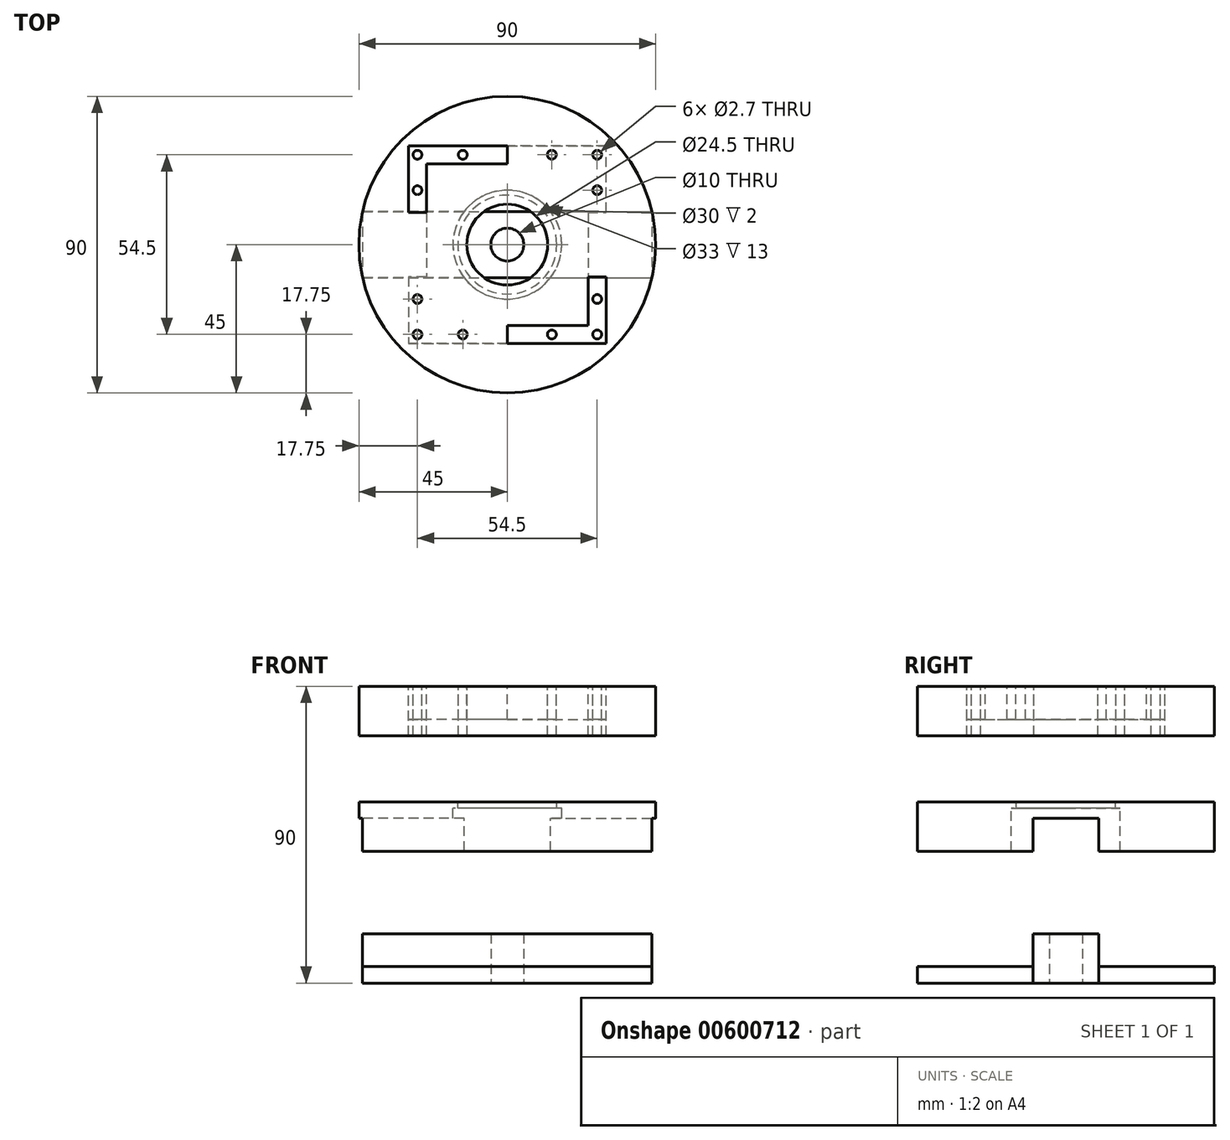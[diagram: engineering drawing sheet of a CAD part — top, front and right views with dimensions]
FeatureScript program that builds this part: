
annotation { "Feature Type Name" : "Feature", "Feature Type Description" : "" }
export const myFeature = defineFeature(function(context is Context, id is Id, definition is map)
    precondition{}
    {
        {
            var Q0;
            Q0=qCreatedBy(makeId("Top.planeOp"),FACE);
            var sketch = newSketch(context, id + "F0", { "sketchPlane" : qUnion([Q0])});
            skLineSegment(sketch, "E0.bottom", {"start": v(12.25, 0) * mm, "end": v(24.5, 0) * mm});
            skLineSegment(sketch, "E0.top", {"start": v(0, 24.5) * mm, "end": v(24.5, 24.5) * mm});
            skLineSegment(sketch, "E0.left", {"start": v(0, 12.25) * mm, "end": v(0, 24.5) * mm});
            skLineSegment(sketch, "E0.right", {"start": v(24.5, 0) * mm, "end": v(24.5, 24.5) * mm});
            skLineSegment(sketch, "E1", {"start": v(0, 24.5) * mm, "end": v(0, 30) * mm});
            skLineSegment(sketch, "E2", {"start": v(0, 30) * mm, "end": v(30, 30) * mm});
            skLineSegment(sketch, "E3", {"start": v(30, 30) * mm, "end": v(30, 9.75) * mm});
            skLineSegment(sketch, "E4", {"start": v(30, 9.75) * mm, "end": v(24.5, 9.75) * mm});
            skCircle(sketch, "E5", {"center": v(0, 0) * mm, "radius": 12.25 * mm});
            skLineSegment(sketch, "E6", {"start": v(0, 27.25) * mm, "end": v(38.5, 27.25) * mm, "construction": true});
            skLineSegment(sketch, "E7", {"start": v(27.25, 9.75) * mm, "end": v(27.25, 36.61) * mm, "construction": true});
            skCircle(sketch, "E8", {"center": v(27.25, 27.25) * mm, "radius": 1.35 * mm});
            skCircle(sketch, "E9", {"center": v(27.25, 16.5) * mm, "radius": 1.35 * mm});
            skCircle(sketch, "E10", {"center": v(13.5, 27.25) * mm, "radius": 1.35 * mm});
            skLineSegment(sketch, "E11.MirrorCS", {"start": v(-30, 30) * mm, "end": v(-30, 9.75) * mm});
            skLineSegment(sketch, "E12.MirrorCS", {"start": v(-24.5, 0) * mm, "end": v(-24.5, 24.5) * mm});
            skLineSegment(sketch, "E13.MirrorCS", {"start": v(-30, 9.75) * mm, "end": v(-24.5, 9.75) * mm});
            skCircle(sketch, "E14.MirrorC", {"center": v(-27.25, 16.5) * mm, "radius": 1.35 * mm});
            skCircle(sketch, "E15.MirrorC", {"center": v(-27.25, 27.25) * mm, "radius": 1.35 * mm});
            skCircle(sketch, "E16.MirrorC", {"center": v(-13.5, 27.25) * mm, "radius": 1.35 * mm});
            skLineSegment(sketch, "E17.MirrorCS", {"start": v(0, 30) * mm, "end": v(-30, 30) * mm});
            skLineSegment(sketch, "E18.MirrorCS", {"start": v(0, 24.5) * mm, "end": v(-24.5, 24.5) * mm});
            skLineSegment(sketch, "E19.MirrorCS", {"start": v(-30, -9.75) * mm, "end": v(-24.5, -9.75) * mm});
            skCircle(sketch, "E20.MirrorC", {"center": v(-27.25, -27.25) * mm, "radius": 1.35 * mm});
            skLineSegment(sketch, "E21.MirrorCS", {"start": v(0, -30) * mm, "end": v(-30, -30) * mm});
            skLineSegment(sketch, "E22.MirrorCS", {"start": v(0, -24.5) * mm, "end": v(-24.5, -24.5) * mm});
            skCircle(sketch, "E23.MirrorC", {"center": v(27.25, -16.5) * mm, "radius": 1.35 * mm});
            skCircle(sketch, "E24.MirrorC", {"center": v(-13.5, -27.25) * mm, "radius": 1.35 * mm});
            skCircle(sketch, "E25.MirrorC", {"center": v(27.25, -27.25) * mm, "radius": 1.35 * mm});
            skLineSegment(sketch, "E26.MirrorCS", {"start": v(30, -9.75) * mm, "end": v(24.5, -9.75) * mm});
            skCircle(sketch, "E27.MirrorC", {"center": v(-27.25, -16.5) * mm, "radius": 1.35 * mm});
            skCircle(sketch, "E28.MirrorC", {"center": v(13.5, -27.25) * mm, "radius": 1.35 * mm});
            skLineSegment(sketch, "E29.MirrorCS", {"start": v(-30, -30) * mm, "end": v(-30, -9.75) * mm});
            skLineSegment(sketch, "E30.MirrorCS", {"start": v(-24.5, 0) * mm, "end": v(-24.5, -24.5) * mm});
            skLineSegment(sketch, "E31.MirrorCS", {"start": v(30, -30) * mm, "end": v(30, -9.75) * mm});
            skLineSegment(sketch, "E32.MirrorCS", {"start": v(0, -30) * mm, "end": v(30, -30) * mm});
            skLineSegment(sketch, "E33.MirrorCS", {"start": v(0, -24.5) * mm, "end": v(24.5, -24.5) * mm});
            skLineSegment(sketch, "E34.MirrorCS", {"start": v(0, -24.5) * mm, "end": v(0, -30) * mm});
            skLineSegment(sketch, "E35.MirrorCS", {"start": v(24.5, 0) * mm, "end": v(24.5, -24.5) * mm});
            skSolve(sketch);
        }
        {
            var Q0;
            Q0=qCreatedBy(makeId("Top.planeOp"),FACE);
            var sketch = newSketch(context, id + "F1", { "sketchPlane" : qUnion([Q0])});
            skCircle(sketch, "E36", {"center": v(0, 0) * mm, "radius": 45 * mm});
            skSolve(sketch);
        }
        {
            var Q0;
            Q0=makeQuery(id+"F1.imprint","IMPRINT",FACE,{"disambiguationData":[TD([[makeQuery(id+"F1.imprint","IMPRINT",EDGE,{"derivedFrom":sQuery(id+"F1.wireOp",EDGE,"E36")}),1.0]])]});
            extrude(context, id + "F2", {"entities" : qUnion([Q0]), "depth" : 10 * mm, "offsetDistance" : 25 * mm, "hasSecondDirection" : true, "secondDirectionOppositeDirection" : true, "secondDirectionDepth" : 5 * mm});
        }
        {
            var Q0;
            {var subQ1=sQuery(id+"F0.wireOp",EDGE,"E0.top");Q0=makeQuery(id+"F0.imprint","IMPRINT",FACE,{"disambiguationData":[TD([[makeQuery(id+"F0.imprint","IMPRINT",EDGE,{"derivedFrom":subQ1}),1.0]])]});}
            var Q1;
            {var subQ1=sQuery(id+"F0.wireOp",EDGE,"E0.bottom");Q1=makeQuery(id+"F0.imprint","IMPRINT",FACE,{"disambiguationData":[TD([[makeQuery(id+"F0.imprint","IMPRINT",EDGE,{"derivedFrom":subQ1}),1.0]])]});}
            var Q2;
            {var subQ7=sQuery(id+"F0.wireOp",EDGE,"E0.bottom");Q2=makeQuery(id+"F0.imprint","IMPRINT",FACE,{"disambiguationData":[TD([[makeQuery(id+"F0.imprint","IMPRINT",EDGE,{"derivedFrom":subQ7}),-1.0]])]});}
            var Q3;
            Q3=makeQuery(id+"F0.imprint","IMPRINT",FACE,{"disambiguationData":[TD([[makeQuery(id+"F0.imprint","IMPRINT",EDGE,{"derivedFrom":sQuery(id+"F0.wireOp",EDGE,"E23.MirrorC")}),1.0]])]});
            var Q4;
            {var subQ2=sQuery(id+"F0.wireOp",EDGE,"E19.MirrorCS");Q4=makeQuery(id+"F0.imprint","IMPRINT",FACE,{"disambiguationData":[TD([[makeQuery(id+"F0.imprint","IMPRINT",EDGE,{"derivedFrom":subQ2}),-1.0]])]});}
            var Q5;
            Q5=makeQuery(id+"F0.imprint","IMPRINT",FACE,{"disambiguationData":[TD([[makeQuery(id+"F0.imprint","IMPRINT",EDGE,{"derivedFrom":sQuery(id+"F0.wireOp",EDGE,"E1")}),1.0]])]});
            var Q6;
            Q6=makeQuery(id+"F2.opExtrude","SWEPT_BODY",BODY,{"disambiguationData":[OSD([sQuery(id+"F1.wireOp",EDGE,"E36")])]});
            extrude(context, id + "F3", {"entities" : qUnion([Q0, Q1, Q2, Q3, Q4, Q5]), "operationType" : NewBodyOperationType.REMOVE, "endBound" : BoundingType.UP_TO_BODY, "oppositeDirection" : true, "depth" : 25 * mm, "endBoundEntityBody" : qUnion([Q6]), "offsetDistance" : 25 * mm});
        }
        {
            var Q0;
            Q0=makeQuery(id+"F0.imprint","IMPRINT",FACE,{"disambiguationData":[TD([[makeQuery(id+"F0.imprint","IMPRINT",EDGE,{"derivedFrom":sQuery(id+"F0.wireOp",EDGE,"E25.MirrorC")}),-1.0]])]});
            var Q1;
            Q1=makeQuery(id+"F0.imprint","IMPRINT",FACE,{"disambiguationData":[TD([[makeQuery(id+"F0.imprint","IMPRINT",EDGE,{"derivedFrom":sQuery(id+"F0.wireOp",EDGE,"E23.MirrorC")}),-1.0]])]});
            var Q2;
            {var subQ0=sQuery(id+"F0.wireOp",EDGE,"E5");var subQ1=makeQuery(id+"F0.imprint","INTERSECT",VERTEX,{"derivedFrom":[sQuery(id+"F0.wireOp",EDGE,"E0.bottom"),subQ0]});Q2=makeQuery(id+"F0.imprint","IMPRINT",FACE,{"disambiguationData":[TD([[makeQuery(id+"F0.imprint","IMPRINT",EDGE,{"disambiguationData":[TD([[subQ1,-1.0]])],"derivedFrom":subQ0}),1.0]])]});}
            var Q3;
            Q3=makeQuery(id+"F0.imprint","IMPRINT",FACE,{"disambiguationData":[TD([[makeQuery(id+"F0.imprint","IMPRINT",EDGE,{"derivedFrom":sQuery(id+"F0.wireOp",EDGE,"E9")}),1.0]])]});
            var Q4;
            Q4=makeQuery(id+"F0.imprint","IMPRINT",FACE,{"disambiguationData":[TD([[makeQuery(id+"F0.imprint","IMPRINT",EDGE,{"derivedFrom":sQuery(id+"F0.wireOp",EDGE,"E8")}),1.0]])]});
            var Q5;
            Q5=makeQuery(id+"F0.imprint","IMPRINT",FACE,{"disambiguationData":[TD([[makeQuery(id+"F0.imprint","IMPRINT",EDGE,{"derivedFrom":sQuery(id+"F0.wireOp",EDGE,"E28.MirrorC")}),-1.0]])]});
            var Q6;
            Q6=makeQuery(id+"F0.imprint","IMPRINT",FACE,{"disambiguationData":[TD([[makeQuery(id+"F0.imprint","IMPRINT",EDGE,{"derivedFrom":sQuery(id+"F0.wireOp",EDGE,"E10")}),1.0]])]});
            var Q7;
            Q7=makeQuery(id+"F0.imprint","IMPRINT",FACE,{"disambiguationData":[TD([[makeQuery(id+"F0.imprint","IMPRINT",EDGE,{"derivedFrom":sQuery(id+"F0.wireOp",EDGE,"E27.MirrorC")}),1.0]])]});
            var Q8;
            Q8=makeQuery(id+"F0.imprint","IMPRINT",FACE,{"disambiguationData":[TD([[makeQuery(id+"F0.imprint","IMPRINT",EDGE,{"derivedFrom":sQuery(id+"F0.wireOp",EDGE,"E20.MirrorC")}),1.0]])]});
            var Q9;
            Q9=makeQuery(id+"F0.imprint","IMPRINT",FACE,{"disambiguationData":[TD([[makeQuery(id+"F0.imprint","IMPRINT",EDGE,{"derivedFrom":sQuery(id+"F0.wireOp",EDGE,"E24.MirrorC")}),1.0]])]});
            var Q10;
            Q10=makeQuery(id+"F0.imprint","IMPRINT",FACE,{"disambiguationData":[TD([[makeQuery(id+"F0.imprint","IMPRINT",EDGE,{"derivedFrom":sQuery(id+"F0.wireOp",EDGE,"E14.MirrorC")}),-1.0]])]});
            var Q11;
            Q11=makeQuery(id+"F0.imprint","IMPRINT",FACE,{"disambiguationData":[TD([[makeQuery(id+"F0.imprint","IMPRINT",EDGE,{"derivedFrom":sQuery(id+"F0.wireOp",EDGE,"E15.MirrorC")}),-1.0]])]});
            var Q12;
            Q12=makeQuery(id+"F0.imprint","IMPRINT",FACE,{"disambiguationData":[TD([[makeQuery(id+"F0.imprint","IMPRINT",EDGE,{"derivedFrom":sQuery(id+"F0.wireOp",EDGE,"E16.MirrorC")}),-1.0]])]});
            extrude(context, id + "F4", {"entities" : qUnion([Q0, Q1, Q2, Q3, Q4, Q5, Q6, Q7, Q8, Q9, Q10, Q11, Q12]), "operationType" : NewBodyOperationType.REMOVE, "endBound" : BoundingType.THROUGH_ALL, "oppositeDirection" : true, "depth" : 25 * mm, "offsetDistance" : 25 * mm, "hasSecondDirection" : true, "secondDirectionBound" : BoundingType.THROUGH_ALL, "secondDirectionOppositeDirection" : false, "secondDirectionDepth" : 25 * mm});
        }
        {
            var Q0;
            Q0=qCreatedBy(makeId("Top.planeOp"),FACE);
            cPlane(context, id + "F5", {"entities" : qUnion([Q0]), "cplaneType" : CPlaneType.OFFSET, "offset" : 25 * mm, "oppositeDirection" : true, "width" : 150 * mm, "height" : 150 * mm});
        }
        {
            var Q0;
            Q0=qCreatedBy(id+"F5.planeOp",FACE);
            var sketch = newSketch(context, id + "F6", { "sketchPlane" : qUnion([Q0])});
            skCircle(sketch, "E37", {"center": v(0, 0) * mm, "radius": 16.5 * mm});
            skLineSegment(sketch, "E38.bottom", {"start": v(-13.12, -10) * mm, "end": v(-43.87, -10) * mm});
            skLineSegment(sketch, "E38.top", {"start": v(-13.12, 10) * mm, "end": v(-43.87, 10) * mm});
            skCircle(sketch, "E39", {"center": v(0, 0) * mm, "radius": 15 * mm});
            skCircle(sketch, "E40", {"center": v(0, 0) * mm, "radius": 45 * mm});
            skLineSegment(sketch, "E41.MirrorCS", {"start": v(13.12, 10) * mm, "end": v(43.87, 10) * mm});
            skLineSegment(sketch, "E42.MirrorCS", {"start": v(13.12, -10) * mm, "end": v(43.87, -10) * mm});
            skSolve(sketch);
        }
        {
            var Q0;
            Q0=makeQuery(id+"F6.imprint","IMPRINT",FACE,{"disambiguationData":[TD([[makeQuery(id+"F6.imprint","IMPRINT",EDGE,{"derivedFrom":sQuery(id+"F6.wireOp",EDGE,"E39")}),-1.0]])]});
            extrude(context, id + "F7", {"entities" : qUnion([Q0]), "oppositeDirection" : true, "depth" : 2 * mm, "offsetDistance" : 25 * mm});
        }
        {
            var Q0;
            {var subQ0=sQuery(id+"F6.wireOp",EDGE,"E41.MirrorCS");Q0=makeQuery(id+"F6.imprint","IMPRINT",FACE,{"disambiguationData":[TD([[makeQuery(id+"F6.imprint","IMPRINT",EDGE,{"derivedFrom":subQ0}),-1.0]])]});}
            var Q1;
            {var subQ0=sQuery(id+"F6.wireOp",EDGE,"E38.bottom");Q1=makeQuery(id+"F6.imprint","IMPRINT",FACE,{"disambiguationData":[TD([[makeQuery(id+"F6.imprint","IMPRINT",EDGE,{"derivedFrom":subQ0}),-1.0]])]});}
            extrude(context, id + "F8", {"entities" : qUnion([Q0, Q1]), "operationType" : NewBodyOperationType.ADD, "oppositeDirection" : true, "depth" : 5 * mm, "offsetDistance" : 25 * mm});
        }
        {
            var Q0;
            {var subQ0=sQuery(id+"F6.wireOp",EDGE,"E38.top");Q0=makeQuery(id+"F6.imprint","IMPRINT",FACE,{"disambiguationData":[TD([[makeQuery(id+"F6.imprint","IMPRINT",EDGE,{"derivedFrom":subQ0}),-1.0]])]});}
            var Q1;
            {var subQ0=sQuery(id+"F6.wireOp",EDGE,"E38.bottom");Q1=makeQuery(id+"F6.imprint","IMPRINT",FACE,{"disambiguationData":[TD([[makeQuery(id+"F6.imprint","IMPRINT",EDGE,{"derivedFrom":subQ0}),1.0]])]});}
            extrude(context, id + "F9", {"entities" : qUnion([Q0, Q1]), "operationType" : NewBodyOperationType.ADD, "oppositeDirection" : true, "depth" : 15 * mm, "offsetDistance" : 25 * mm});
        }
        {
            var Q0;
            Q0=qCreatedBy(makeId("Top.planeOp"),FACE);
            cPlane(context, id + "F10", {"entities" : qUnion([Q0]), "cplaneType" : CPlaneType.OFFSET, "offset" : 75 * mm, "oppositeDirection" : true, "width" : 150 * mm, "height" : 150 * mm});
        }
        {
            var Q0;
            Q0=qCreatedBy(id+"F10.planeOp",FACE);
            var sketch = newSketch(context, id + "F11", { "sketchPlane" : qUnion([Q0])});
            skCircle(sketch, "E43", {"center": v(0, 0) * mm, "radius": 45 * mm});
            skLineSegment(sketch, "E44.bottom", {"start": v(-43.87, 10) * mm, "end": v(43.87, 10) * mm});
            skLineSegment(sketch, "E44.top", {"start": v(-43.87, -10) * mm, "end": v(43.87, -10) * mm});
            skLineSegment(sketch, "E44.left", {"start": v(-43.87, 10) * mm, "end": v(-43.87, -10) * mm});
            skLineSegment(sketch, "E44.right", {"start": v(43.87, 10) * mm, "end": v(43.87, -10) * mm});
            skCircle(sketch, "E45", {"center": v(0, 0) * mm, "radius": 5 * mm});
            skSolve(sketch);
        }
        {
            var Q0;
            Q0=makeQuery(id+"F11.imprint","IMPRINT",FACE,{"disambiguationData":[TD([[makeQuery(id+"F11.imprint","IMPRINT",EDGE,{"derivedFrom":sQuery(id+"F11.wireOp",EDGE,"E44.bottom")}),-1.0]])]});
            extrude(context, id + "F12", {"entities" : qUnion([Q0]), "depth" : 10 * mm, "offsetDistance" : 25 * mm, "hasSecondDirection" : true, "secondDirectionOppositeDirection" : true, "secondDirectionDepth" : 5 * mm});
        }
        {
            var Q0;
            {var subQ0=sQuery(id+"F11.wireOp",EDGE,"E44.bottom");Q0=makeQuery(id+"F11.imprint","IMPRINT",FACE,{"disambiguationData":[TD([[makeQuery(id+"F11.imprint","IMPRINT",EDGE,{"derivedFrom":subQ0}),1.0]])]});}
            var Q1;
            {var subQ0=sQuery(id+"F11.wireOp",EDGE,"E44.top");Q1=makeQuery(id+"F11.imprint","IMPRINT",FACE,{"disambiguationData":[TD([[makeQuery(id+"F11.imprint","IMPRINT",EDGE,{"derivedFrom":subQ0}),-1.0]])]});}
            extrude(context, id + "F13", {"entities" : qUnion([Q0, Q1]), "operationType" : NewBodyOperationType.ADD, "oppositeDirection" : true, "depth" : 5 * mm, "offsetDistance" : 25 * mm});
        }
    });
